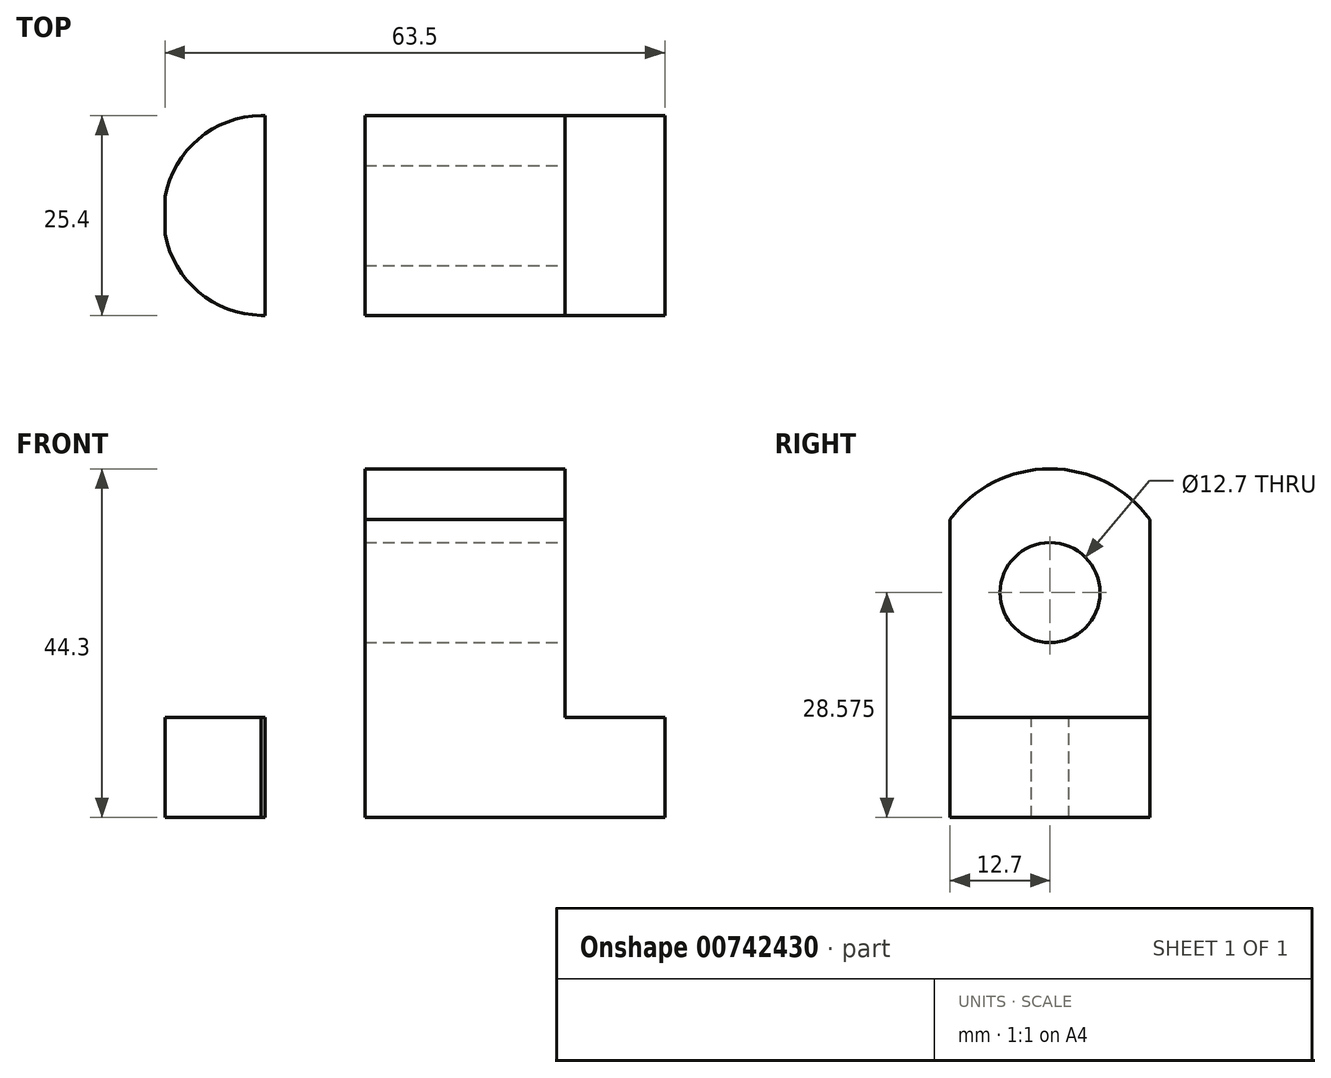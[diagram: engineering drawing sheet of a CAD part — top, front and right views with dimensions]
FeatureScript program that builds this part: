
annotation { "Feature Type Name" : "Feature", "Feature Type Description" : "" }
export const myFeature = defineFeature(function(context is Context, id is Id, definition is map)
    precondition{}
    {
        {
            var Q0;
            Q0=qCreatedBy(makeId("Front.planeOp"),FACE);
            var sketch = newSketch(context, id + "F0", { "sketchPlane" : qUnion([Q0])});
            skLineSegment(sketch, "E0", {"start": v(0, 0) * mm, "end": v(0, 44.45) * mm});
            skLineSegment(sketch, "E1", {"start": v(0, 44.45) * mm, "end": v(76.2, 44.45) * mm});
            skLineSegment(sketch, "E2", {"start": v(76.2, 44.45) * mm, "end": v(76.2, 0) * mm});
            skLineSegment(sketch, "E3", {"start": v(76.2, 0) * mm, "end": v(0, 0) * mm});
            skSolve(sketch);
        }
        {
            var Q0;
            Q0 = qSketchRegion(id + "F0", true);
            extrude(context, id + "F1", {"entities" : qUnion([Q0]), "depth" : 25.4 * mm, "offsetDistance" : 25.4 * mm});
        }
        {
            var Q0;
            Q0=makeQuery(id+"F1.opExtrude","CAP_FACE",FACE,{"disambiguationData":[OSD([sQuery(id+"F0.wireOp",EDGE,"E0"),sQuery(id+"F0.wireOp",EDGE,"E1"),sQuery(id+"F0.wireOp",EDGE,"E2"),sQuery(id+"F0.wireOp",EDGE,"E3")])],"isStart":false});
            var sketch = newSketch(context, id + "F2", { "sketchPlane" : qUnion([Q0])});
            skLineSegment(sketch, "E4", {"start": v(25.4, 44.45) * mm, "end": v(25.4, 12.7) * mm});
            skLineSegment(sketch, "E5", {"start": v(25.4, 12.7) * mm, "end": v(0, 12.7) * mm});
            skLineSegment(sketch, "E6", {"start": v(50.8, 44.45) * mm, "end": v(50.8, 12.7) * mm});
            skLineSegment(sketch, "E7", {"start": v(50.8, 12.7) * mm, "end": v(76.2, 12.7) * mm});
            skSolve(sketch);
        }
        {
            var Q0;
            {var subQ0=sQuery(id+"F2.wireOp",EDGE,"E4");Q0=makeQuery(id+"F2.imprint","IMPRINT",FACE,{"disambiguationData":[TD([[makeQuery(id+"F2.imprint","IMPRINT",EDGE,{"derivedFrom":subQ0}),-1.0]])]});}
            var Q1;
            {var subQ0=sQuery(id+"F2.wireOp",EDGE,"E6");Q1=makeQuery(id+"F2.imprint","IMPRINT",FACE,{"disambiguationData":[TD([[makeQuery(id+"F2.imprint","IMPRINT",EDGE,{"derivedFrom":subQ0}),1.0]])]});}
            extrude(context, id + "F3", {"entities" : qUnion([Q0, Q1]), "operationType" : NewBodyOperationType.REMOVE, "oppositeDirection" : true, "depth" : 25.4 * mm, "offsetDistance" : 25.4 * mm});
        }
        {
            var Q0;
            Q0=makeQuery(id+"F3.boolean.opBoolean","COPY",FACE,{"derivedFrom":makeQuery(id+"F3.opExtrude","SWEPT_FACE",FACE,{"disambiguationData":[OSD([sQuery(id+"F2.wireOp",EDGE,"E6")])]})});
            var sketch = newSketch(context, id + "F4", { "sketchPlane" : qUnion([Q0])});
            skLineSegment(sketch, "E8", {"start": v(-12.7, 44.45) * mm, "end": v(-12.7, 12.7) * mm});
            skLineSegment(sketch, "E9", {"start": v(-25.4, 28.58) * mm, "end": v(0, 28.58) * mm});
            skCircle(sketch, "E10", {"center": v(-12.7, 28.58) * mm, "radius": 15.73 * mm});
            skCircle(sketch, "E11", {"center": v(-12.7, 28.58) * mm, "radius": 6.35 * mm});
            skSolve(sketch);
        }
        {
            var Q0;
            {var subQ0=sQuery(id+"F4.wireOp",EDGE,"E11");var subQ1=sQuery(id+"F4.wireOp",EDGE,"E8");var subQ2=makeQuery(id+"F4.imprint","INTERSECT",VERTEX,{"disambiguationData":[OD(0.0)],"derivedFrom":[subQ1,subQ0]});Q0=makeQuery(id+"F4.imprint","IMPRINT",FACE,{"disambiguationData":[TD([[makeQuery(id+"F4.imprint","IMPRINT",EDGE,{"disambiguationData":[TD([[subQ2,-1.0]])],"derivedFrom":subQ1}),-1.0]])]});}
            var Q1;
            {var subQ0=sQuery(id+"F4.wireOp",EDGE,"E11");var subQ1=sQuery(id+"F4.wireOp",EDGE,"E8");var subQ2=makeQuery(id+"F4.imprint","INTERSECT",VERTEX,{"disambiguationData":[OD(0.0)],"derivedFrom":[subQ1,subQ0]});Q1=makeQuery(id+"F4.imprint","IMPRINT",FACE,{"disambiguationData":[TD([[makeQuery(id+"F4.imprint","IMPRINT",EDGE,{"disambiguationData":[TD([[subQ2,-1.0]])],"derivedFrom":subQ1}),1.0]])]});}
            var Q2;
            {var subQ0=sQuery(id+"F4.wireOp",EDGE,"E9");var subQ1=sQuery(id+"F4.wireOp",EDGE,"E8");var subQ2=makeQuery(id+"F4.imprint","INTERSECT",VERTEX,{"derivedFrom":[subQ1,subQ0]});Q2=makeQuery(id+"F4.imprint","IMPRINT",FACE,{"disambiguationData":[TD([[makeQuery(id+"F4.imprint","IMPRINT",EDGE,{"disambiguationData":[TD([[subQ2,-1.0]])],"derivedFrom":subQ1}),1.0]])]});}
            var Q3;
            {var subQ0=sQuery(id+"F4.wireOp",EDGE,"E9");var subQ1=sQuery(id+"F4.wireOp",EDGE,"E8");var subQ2=makeQuery(id+"F4.imprint","INTERSECT",VERTEX,{"derivedFrom":[subQ1,subQ0]});Q3=makeQuery(id+"F4.imprint","IMPRINT",FACE,{"disambiguationData":[TD([[makeQuery(id+"F4.imprint","IMPRINT",EDGE,{"disambiguationData":[TD([[subQ2,-1.0]])],"derivedFrom":subQ1}),-1.0]])]});}
            var Q4;
            {var subQ0=sQuery(id+"F4.wireOp",EDGE,"E8");var subQ4=sQuery(id+"F4.wireOp",EDGE,"E10");var subQ5=makeQuery(id+"F4.imprint","INTERSECT",VERTEX,{"disambiguationData":[OD(0.0)],"derivedFrom":[subQ0,subQ4]});Q4=makeQuery(id+"F4.imprint","IMPRINT",FACE,{"disambiguationData":[TD([[makeQuery(id+"F4.imprint","IMPRINT",EDGE,{"disambiguationData":[TD([[subQ5,-1.0]])],"derivedFrom":subQ4}),-1.0]])]});}
            var Q5;
            {var subQ0=sQuery(id+"F4.wireOp",EDGE,"E8");var subQ4=sQuery(id+"F4.wireOp",EDGE,"E10");var subQ5=makeQuery(id+"F4.imprint","INTERSECT",VERTEX,{"disambiguationData":[OD(0.0)],"derivedFrom":[subQ0,subQ4]});Q5=makeQuery(id+"F4.imprint","IMPRINT",FACE,{"disambiguationData":[TD([[makeQuery(id+"F4.imprint","IMPRINT",EDGE,{"disambiguationData":[TD([[subQ5,1.0]])],"derivedFrom":subQ4}),-1.0]])]});}
            extrude(context, id + "F5", {"entities" : qUnion([Q0, Q1, Q2, Q3, Q4, Q5]), "operationType" : NewBodyOperationType.REMOVE, "oppositeDirection" : true, "depth" : 25.4 * mm, "offsetDistance" : 25.4 * mm});
        }
        {
            var Q0;
            Q0=makeQuery(id+"F3.boolean.opBoolean","COPY",FACE,{"derivedFrom":makeQuery(id+"F3.opExtrude","SWEPT_FACE",FACE,{"disambiguationData":[OSD([sQuery(id+"F2.wireOp",EDGE,"E5")])]})});
            var sketch = newSketch(context, id + "F6", { "sketchPlane" : qUnion([Q0])});
            skLineSegment(sketch, "E12", {"start": v(0, -12.7) * mm, "end": v(25.4, -12.7) * mm});
            skLineSegment(sketch, "E13", {"start": v(12.7, 0) * mm, "end": v(12.7, -25.4) * mm});
            skCircle(sketch, "E14", {"center": v(12.7, -12.7) * mm, "radius": 6.35 * mm});
            skArc(sketch, "E15", {"start": v(12.7, 0) * mm, "mid": v(-0.22, -12.7) * mm, "end": v(12.7, -25.4) * mm});
            skSolve(sketch);
        }
        {
            var Q0;
            {var subQ0=sQuery(id+"F6.wireOp",EDGE,"E14");var subQ1=sQuery(id+"F6.wireOp",EDGE,"E12");var subQ2=makeQuery(id+"F6.imprint","INTERSECT",VERTEX,{"disambiguationData":[OD(0.0)],"derivedFrom":[subQ1,subQ0]});Q0=makeQuery(id+"F6.imprint","IMPRINT",FACE,{"disambiguationData":[TD([[makeQuery(id+"F6.imprint","IMPRINT",EDGE,{"disambiguationData":[TD([[subQ2,-1.0]])],"derivedFrom":subQ1}),1.0]])]});}
            var Q1;
            {var subQ0=sQuery(id+"F6.wireOp",EDGE,"E13");var subQ1=sQuery(id+"F6.wireOp",EDGE,"E12");var subQ2=makeQuery(id+"F6.imprint","INTERSECT",VERTEX,{"derivedFrom":[subQ1,subQ0]});Q1=makeQuery(id+"F6.imprint","IMPRINT",FACE,{"disambiguationData":[TD([[makeQuery(id+"F6.imprint","IMPRINT",EDGE,{"disambiguationData":[TD([[subQ2,-1.0]])],"derivedFrom":subQ1}),1.0]])]});}
            var Q2;
            {var subQ0=sQuery(id+"F6.wireOp",EDGE,"E14");var subQ1=sQuery(id+"F6.wireOp",EDGE,"E12");var subQ2=makeQuery(id+"F6.imprint","INTERSECT",VERTEX,{"disambiguationData":[OD(0.0)],"derivedFrom":[subQ1,subQ0]});Q2=makeQuery(id+"F6.imprint","IMPRINT",FACE,{"disambiguationData":[TD([[makeQuery(id+"F6.imprint","IMPRINT",EDGE,{"disambiguationData":[TD([[subQ2,-1.0]])],"derivedFrom":subQ1}),-1.0]])]});}
            var Q3;
            {var subQ0=sQuery(id+"F6.wireOp",EDGE,"E13");var subQ1=sQuery(id+"F6.wireOp",EDGE,"E12");var subQ2=makeQuery(id+"F6.imprint","INTERSECT",VERTEX,{"derivedFrom":[subQ1,subQ0]});Q3=makeQuery(id+"F6.imprint","IMPRINT",FACE,{"disambiguationData":[TD([[makeQuery(id+"F6.imprint","IMPRINT",EDGE,{"disambiguationData":[TD([[subQ2,-1.0]])],"derivedFrom":subQ1}),-1.0]])]});}
            var Q4;
            {var subQ0=sQuery(id+"F6.wireOp",EDGE,"E15");var subQ1=sQuery(id+"F2.wireOp",EDGE,"E5");var subQ2=makeQuery(id+"F3.boolean.opBoolean","COPY",EDGE,{"derivedFrom":makeQuery(id+"F3.opExtrude","CAP_EDGE",EDGE,{"disambiguationData":[OSD([subQ1])],"isStart":false})});var subQ3=makeQuery(id+"F6.imprint","INTERSECT",VERTEX,{"derivedFrom":[subQ2,subQ0]});Q4=makeQuery(id+"F6.imprint","IMPRINT",FACE,{"disambiguationData":[TD([[makeQuery(id+"F6.imprint","IMPRINT",EDGE,{"disambiguationData":[TD([[subQ3,-1.0]])],"derivedFrom":subQ0}),-1.0]])]});}
            var Q5;
            {var subQ0=sQuery(id+"F6.wireOp",EDGE,"E15");var subQ1=sQuery(id+"F2.wireOp",EDGE,"E5");var subQ4=makeQuery(id+"F3.boolean.opBoolean","COPY",EDGE,{"derivedFrom":makeQuery(id+"F3.opExtrude","CAP_EDGE",EDGE,{"disambiguationData":[OSD([subQ1])],"isStart":true})});var subQ5=makeQuery(id+"F6.imprint","INTERSECT",VERTEX,{"derivedFrom":[subQ4,subQ0]});Q5=makeQuery(id+"F6.imprint","IMPRINT",FACE,{"disambiguationData":[TD([[makeQuery(id+"F6.imprint","IMPRINT",EDGE,{"disambiguationData":[TD([[subQ5,1.0]])],"derivedFrom":subQ0}),-1.0]])]});}
            extrude(context, id + "F7", {"entities" : qUnion([Q0, Q1, Q2, Q3, Q4, Q5]), "operationType" : NewBodyOperationType.REMOVE, "oppositeDirection" : true, "depth" : 25.4 * mm, "offsetDistance" : 25.4 * mm});
        }
        {
            var Q0;
            Q0=makeQuery(id+"F3.boolean.opBoolean","COPY",FACE,{"derivedFrom":makeQuery(id+"F3.opExtrude","SWEPT_FACE",FACE,{"disambiguationData":[OSD([sQuery(id+"F2.wireOp",EDGE,"E7")])]})});
            var sketch = newSketch(context, id + "F8", { "sketchPlane" : qUnion([Q0])});
            skLineSegment(sketch, "E16", {"start": v(50.8, -12.7) * mm, "end": v(76.2, -12.7) * mm});
            skLineSegment(sketch, "E17", {"start": v(63.5, 0) * mm, "end": v(63.5, -25.4) * mm});
            skCircle(sketch, "E18", {"center": v(63.5, -12.7) * mm, "radius": 6.35 * mm});
            skArc(sketch, "E19", {"start": v(63.5, -25.4) * mm, "mid": v(76.33, -12.7) * mm, "end": v(63.5, 0) * mm});
            skSolve(sketch);
        }
        {
            var Q0;
            {var subQ0=sQuery(id+"F8.wireOp",EDGE,"E19");var subQ1=sQuery(id+"F2.wireOp",EDGE,"E7");var subQ4=makeQuery(id+"F3.boolean.opBoolean","COPY",EDGE,{"derivedFrom":makeQuery(id+"F3.opExtrude","CAP_EDGE",EDGE,{"disambiguationData":[OSD([subQ1])],"isStart":false})});var subQ5=makeQuery(id+"F8.imprint","INTERSECT",VERTEX,{"derivedFrom":[subQ4,subQ0]});Q0=makeQuery(id+"F8.imprint","IMPRINT",FACE,{"disambiguationData":[TD([[makeQuery(id+"F8.imprint","IMPRINT",EDGE,{"disambiguationData":[TD([[subQ5,1.0]])],"derivedFrom":subQ0}),-1.0]])]});}
            var Q1;
            {var subQ0=sQuery(id+"F8.wireOp",EDGE,"E19");var subQ1=sQuery(id+"F2.wireOp",EDGE,"E7");var subQ2=makeQuery(id+"F3.boolean.opBoolean","COPY",EDGE,{"derivedFrom":makeQuery(id+"F3.opExtrude","CAP_EDGE",EDGE,{"disambiguationData":[OSD([subQ1])],"isStart":true})});var subQ3=makeQuery(id+"F8.imprint","INTERSECT",VERTEX,{"derivedFrom":[subQ2,subQ0]});Q1=makeQuery(id+"F8.imprint","IMPRINT",FACE,{"disambiguationData":[TD([[makeQuery(id+"F8.imprint","IMPRINT",EDGE,{"disambiguationData":[TD([[subQ3,-1.0]])],"derivedFrom":subQ0}),-1.0]])]});}
            var Q2;
            {var subQ0=sQuery(id+"F8.wireOp",EDGE,"E18");var subQ1=sQuery(id+"F8.wireOp",EDGE,"E16");var subQ2=makeQuery(id+"F8.imprint","INTERSECT",VERTEX,{"disambiguationData":[OD(0.0)],"derivedFrom":[subQ1,subQ0]});Q2=makeQuery(id+"F8.imprint","IMPRINT",FACE,{"disambiguationData":[TD([[makeQuery(id+"F8.imprint","IMPRINT",EDGE,{"disambiguationData":[TD([[subQ2,-1.0]])],"derivedFrom":subQ1}),1.0]])]});}
            var Q3;
            {var subQ0=sQuery(id+"F8.wireOp",EDGE,"E17");var subQ1=sQuery(id+"F8.wireOp",EDGE,"E16");var subQ2=makeQuery(id+"F8.imprint","INTERSECT",VERTEX,{"derivedFrom":[subQ1,subQ0]});Q3=makeQuery(id+"F8.imprint","IMPRINT",FACE,{"disambiguationData":[TD([[makeQuery(id+"F8.imprint","IMPRINT",EDGE,{"disambiguationData":[TD([[subQ2,-1.0]])],"derivedFrom":subQ1}),-1.0]])]});}
            var Q4;
            {var subQ0=sQuery(id+"F8.wireOp",EDGE,"E18");var subQ1=sQuery(id+"F8.wireOp",EDGE,"E16");var subQ2=makeQuery(id+"F8.imprint","INTERSECT",VERTEX,{"disambiguationData":[OD(0.0)],"derivedFrom":[subQ1,subQ0]});Q4=makeQuery(id+"F8.imprint","IMPRINT",FACE,{"disambiguationData":[TD([[makeQuery(id+"F8.imprint","IMPRINT",EDGE,{"disambiguationData":[TD([[subQ2,-1.0]])],"derivedFrom":subQ1}),-1.0]])]});}
            var Q5;
            {var subQ0=sQuery(id+"F8.wireOp",EDGE,"E17");var subQ1=sQuery(id+"F8.wireOp",EDGE,"E16");var subQ2=makeQuery(id+"F8.imprint","INTERSECT",VERTEX,{"derivedFrom":[subQ1,subQ0]});Q5=makeQuery(id+"F8.imprint","IMPRINT",FACE,{"disambiguationData":[TD([[makeQuery(id+"F8.imprint","IMPRINT",EDGE,{"disambiguationData":[TD([[subQ2,-1.0]])],"derivedFrom":subQ1}),1.0]])]});}
            extrude(context, id + "F9", {"entities" : qUnion([Q0, Q1, Q2, Q3, Q4, Q5]), "operationType" : NewBodyOperationType.REMOVE, "oppositeDirection" : true, "depth" : 25.4 * mm, "offsetDistance" : 25.4 * mm});
        }
    });
